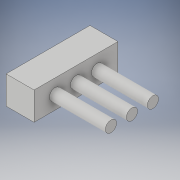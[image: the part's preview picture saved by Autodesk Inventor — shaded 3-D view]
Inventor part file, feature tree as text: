
AUTODESK INVENTOR PART (.ipt)
format: ipt  version: 2019 (Build 230136000, 136)  size: 119,808 bytes
history: native  units: in
note: dims shown in document units (in); Inventor stores cm internally (conversion verified against a paired STEP export)
features: extrude x2, sketch x2
ambient origin geometry x8: Origin, YZ Plane, XZ Plane, XY Plane, X Axis, Y Axis, Z Axis, Center Point
bodies: Solid1 (feature_tree)
feature tree (4):
  extrude  "Extrusion1"  Depth=3.0in
  extrude  "Extrusion2"  Depth=2.0in
  sketch  "Sketch1"  dims[d2=1.0in d3=3.0in]
  sketch  "Sketch2"  dims[d4=1.0in d5=0.0in d6=4.0in d15=0.4in d16=0.4in d17=0.4in d18=1.0in d19=0.5in d21=3.0in d22=1.5in d23=0.75in d24=1.0in d26=0.75in d27=0.5in d28=2.0in d29=0.0in]
